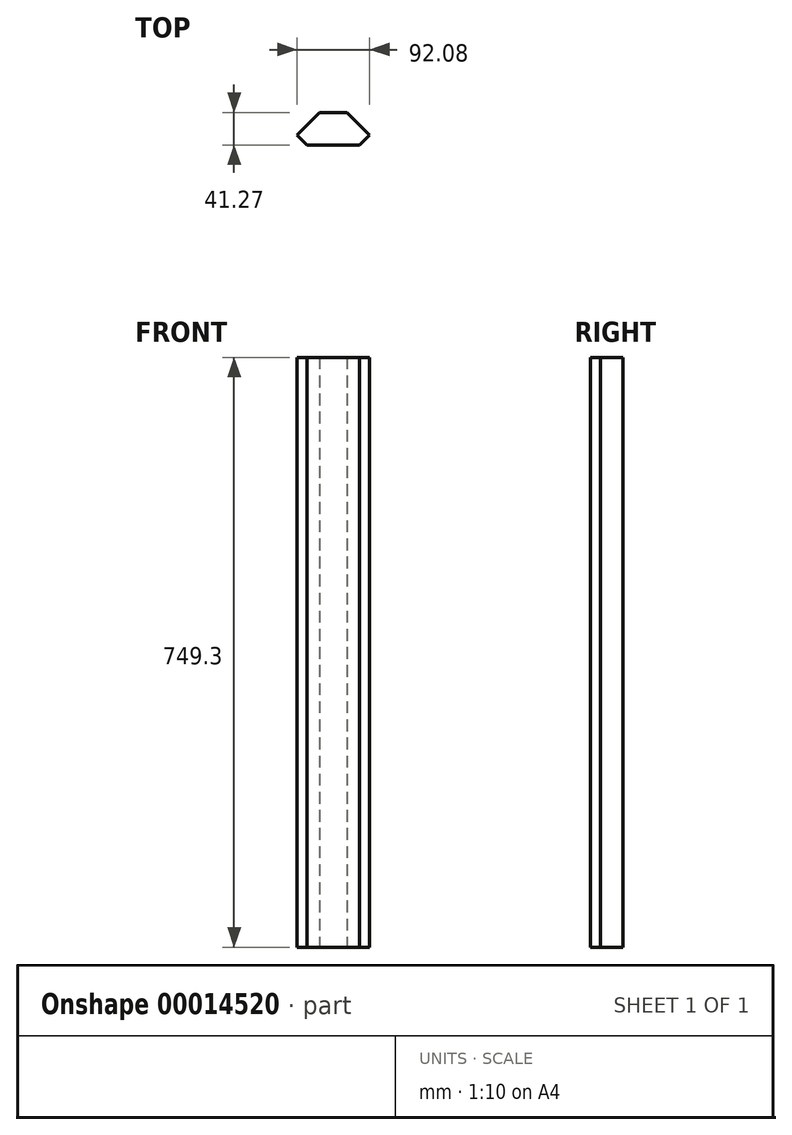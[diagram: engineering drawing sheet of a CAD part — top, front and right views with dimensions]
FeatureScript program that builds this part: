
annotation { "Feature Type Name" : "Feature", "Feature Type Description" : "" }
export const myFeature = defineFeature(function(context is Context, id is Id, definition is map)
    precondition{}
    {
        {
            var Q0;
            Q0=qCreatedBy(makeId("Top.planeOp"),FACE);
            var sketch = newSketch(context, id + "F0", { "sketchPlane" : qUnion([Q0])});
            skLineSegment(sketch, "E0", {"start": v(0, 0) * mm, "end": v(-12.7, 12.7) * mm});
            skLineSegment(sketch, "E1", {"start": v(-12.7, 12.7) * mm, "end": v(15.87, 41.28) * mm});
            skLineSegment(sketch, "E2", {"start": v(15.87, 41.28) * mm, "end": v(50.8, 41.28) * mm});
            skLineSegment(sketch, "E3", {"start": v(50.8, 41.27) * mm, "end": v(79.38, 12.7) * mm});
            skLineSegment(sketch, "E4", {"start": v(79.38, 12.7) * mm, "end": v(66.68, 0) * mm});
            skLineSegment(sketch, "E5", {"start": v(66.68, 0) * mm, "end": v(0, 0) * mm});
            skSolve(sketch);
        }
        {
            var Q0;
            Q0=qSketchRegion(id+"F0",true);
            extrude(context, id + "F1", {"entities" : qUnion([Q0]), "depth" : 749.3 * mm});
        }
    });
